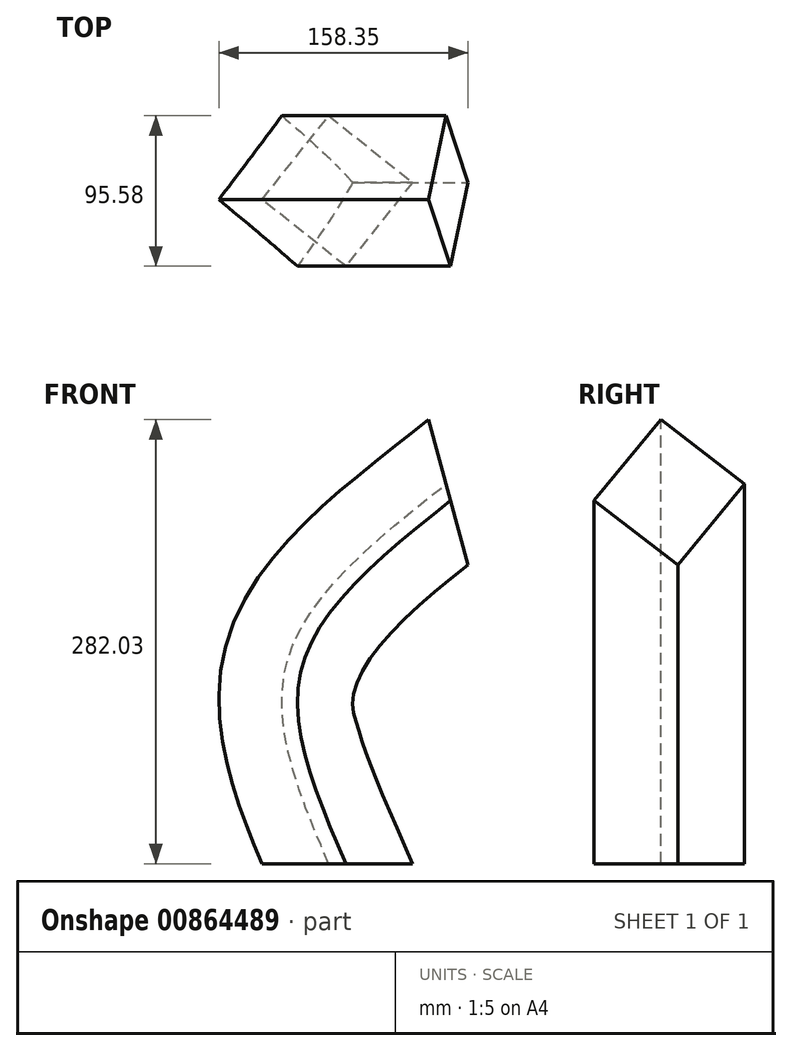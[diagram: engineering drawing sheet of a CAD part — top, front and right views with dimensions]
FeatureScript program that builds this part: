
annotation { "Feature Type Name" : "Feature", "Feature Type Description" : "" }
export const myFeature = defineFeature(function(context is Context, id is Id, definition is map)
    precondition{}
    {
        {
            var Q0;
            Q0=qCreatedBy(makeId("Top.planeOp"),FACE);
            var sketch = newSketch(context, id + "F0", { "sketchPlane" : qUnion([Q0])});
            skCircle(sketch, "E0.cCircle", {"center": v(0, 0) * mm, "radius": 34 * mm, "construction": true});
            skLineSegment(sketch, "E0.0", {"start": v(47.79, 5.42) * mm, "end": v(5.42, -47.79) * mm});
            skLineSegment(sketch, "E0.1", {"start": v(5.42, -47.79) * mm, "end": v(-47.79, -5.42) * mm});
            skLineSegment(sketch, "E0.2", {"start": v(-47.79, -5.42) * mm, "end": v(-5.42, 47.79) * mm});
            skLineSegment(sketch, "E0.3", {"start": v(-5.42, 47.79) * mm, "end": v(47.79, 5.42) * mm});
            skPoint(sketch, "E0.0.midPoint", {"position": v(26.6, -21.19) * mm});
            skSolve(sketch);
        }
        {
            var Q0;
            Q0=qCreatedBy(makeId("Front.planeOp"),FACE);
            var sketch = newSketch(context, id + "F1", { "sketchPlane" : qUnion([Q0])});
            skFitSpline(sketch, "E1", {"points": [v(0, 0) * mm, v(-27.41, 125.77) * mm, v(70.54, 235.93) * mm], "startDerivative": vector(-116.22, 271.77) * mm, "endDerivative": vector(253.12, 200.9) * mm});
            skSolve(sketch);
        }
        {
            var Q0;
            Q0=makeQuery(id+"F0.imprint","IMPRINT",FACE,{"disambiguationData":[TD([[makeQuery(id+"F0.imprint","IMPRINT",EDGE,{"derivedFrom":sQuery(id+"F0.wireOp",EDGE,"E0.0")}),-1.0]])]});
            var Q1;
            Q1=sQuery(id+"F1.wireOp",EDGE,"E1");
            sweep(context, id + "F2", {"profiles" : qUnion([Q0]), "path" : qUnion([Q1])});
        }
    });
